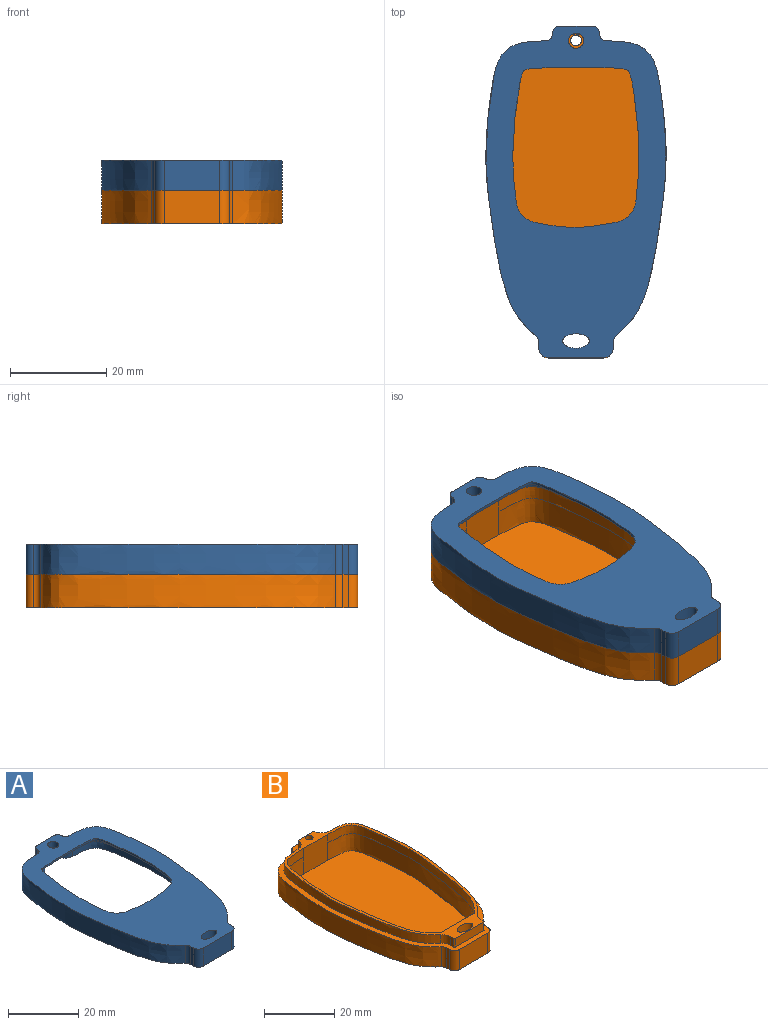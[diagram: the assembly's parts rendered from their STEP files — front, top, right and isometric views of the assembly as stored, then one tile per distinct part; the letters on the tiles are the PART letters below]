
ASSEMBLY  parts=2 mates=1
PART A: 47 faces, bbox 37.5x69.1x6.3 mm
  f0: extruded ~5.57x3.3mm, area 45.3mm2, adj f31,f46
  f1: plane 9.59x2.7mm, normal (0,-1,0), area 25.9mm2, adj f2,f4,f26,f46
  f2: extruded ~56.9x11.37mm, area 179.6mm2, adj f1,f3,f26,f46
  f3: plane 13.49x2.7mm, normal (0,1,0), area 36.4mm2, adj f2,f4,f26,f46
  f4: extruded ~56.9x11.37mm, area 179.6mm2, adj f1,f3,f26,f46
  f5: plane 6.3x1.11mm, normal (-1,0,0), area 7mm2, adj f19,f21,f29,f31
  f6: plane 6.3x1.11mm, normal (1,0,0), area 7mm2, adj f20,f21,f30,f31
  f7: plane 6.3x0.06mm, normal (1,0,0), area 0.4mm2, adj f16,f21,f27,f31
  f8: plane 6.3x0.06mm, normal (-1,0,0), area 0.4mm2, adj f17,f21,f28,f31
  f9: plane 6.3x0.09mm, normal (0.67,-0.74,0), area 0.8mm2, adj f20,f21,f24,f31
  f10: cylinder r=5mm len=4.24mm, axis (0,0,1), area 3.7mm2, adj f11,f15,f26,f31
  f11: extruded ~28x8.43mm, area 20.3mm2, adj f10,f12,f26,f31
  f12: plane 9.48x0.6mm, normal (0,-1,0), area 5.7mm2, adj f11,f13,f26,f31
  f13: extruded ~28.08x8.43mm, area 20.4mm2, adj f12,f14,f26,f31
  f14: cylinder r=5mm len=4.25mm, axis (0,0,1), area 3.7mm2, adj f13,f15,f26,f31
  f15: extruded ~17.03x1.09mm, area 10.3mm2, adj f10,f14,f26,f31
  f16: cylinder r=1.5mm len=6.3mm, axis (0,0,1), area 14.4mm2, adj f7,f21,f24,f31
  f17: cylinder r=1.5mm len=6.3mm, axis (0,0,1), area 14.4mm2, adj f8,f21,f25,f31
  f18: cylinder r=1.59mm len=6.3mm, axis (0,0,1), area 37.9mm2, adj f21,f31,f32,f45,f46
  f19: cylinder r=2mm len=6.3mm, axis (0,0,1), area 10.5mm2, adj f5,f21,f25,f31
  f20: cylinder r=2mm len=6.3mm, axis (0,0,1), area 10.5mm2, adj f6,f9,f21,f31
  f21: plane 69.1x37.55mm, normal (0,0,-1), area 298.6mm2, adj f5,f6,f7,f8,f9,f16,f17,f18
  f22: plane 11.49x6.3mm, normal (0,-1,0), area 72.4mm2, adj f21,f29,f30,f31
  f23: plane 6.69x6.3mm, normal (0,1,0), area 42.2mm2, adj f21,f27,f28,f31
  f24: extruded ~61.37x12.49mm, area 449mm2, adj f9,f16,f21,f31
  f25: extruded ~61.45x12.49mm, area 449.8mm2, adj f17,f19,f21,f31
  f26: plane 56.9x32.93mm, normal (0,0,-1), area 800.2mm2, adj f1,f2,f3,f4,f10,f11,f12,f13
  f27: cylinder r=1.5mm len=6.3mm, axis (0,0,1), area 14.8mm2, adj f7,f21,f23,f31
  f28: cylinder r=1.5mm len=6.3mm, axis (0,0,-1), area 14.8mm2, adj f8,f21,f23,f31
  f29: cylinder r=2mm len=6.3mm, axis (0,0,1), area 19.8mm2, adj f5,f21,f22,f31
  f30: cylinder r=2mm len=6.3mm, axis (0,0,-1), area 19.8mm2, adj f6,f21,f22,f31
  f31: plane 69.1x37.55mm, normal (0,0,1), area 1295.9mm2, adj f0,f5,f6,f7,f8,f9,f10,f11
  f32: plane 3x2.36mm, normal (0,-1,0), area 7.1mm2, adj f18,f21,f33,f46
  f33: cylinder r=3.19mm len=3.06mm, axis (0,0,-1), area 14.2mm2, adj f21,f32,f34,f46
  f34: extruded ~58.43x10.87mm, area 201.8mm2, adj f21,f33,f35,f46
  f35: plane 3x0.09mm, normal (-0.67,0.74,0), area 0.4mm2, adj f21,f34,f36,f46
  f36: cylinder r=3.69mm len=3mm, axis (0,0,-1), area 9.2mm2, adj f21,f35,f37,f46
  f37: plane 3x1.11mm, normal (-1,0,0), area 3.3mm2, adj f21,f36,f38,f46
  f38: cylinder r=0.31mm len=3mm, axis (0,0,-1), area 1.5mm2, adj f21,f37,f39,f46
  f39: plane 11.49x3mm, normal (0,1,0), area 34.5mm2, adj f21,f38,f40,f46
  f40: cylinder r=0.31mm len=3mm, axis (0,0,-1), area 1.5mm2, adj f21,f39,f41,f46
  f41: plane 3x1.11mm, normal (1,0,0), area 3.3mm2, adj f21,f40,f42,f46
  f42: cylinder r=3.69mm len=3mm, axis (0,0,-1), area 9.2mm2, adj f21,f41,f43,f46
  f43: extruded ~58.51x10.87mm, area 202.2mm2, adj f21,f42,f44,f46
  f44: cylinder r=3.19mm len=3.06mm, axis (0,0,-1), area 14.2mm2, adj f21,f43,f45,f46
  f45: plane 3x2.36mm, normal (0,-1,0), area 7.1mm2, adj f18,f21,f44,f46
  f46: plane 65.72x34.17mm, normal (0,0,-1), area 197.1mm2, adj f0,f1,f2,f3,f4,f18,f32,f33
PART B: 42 faces, bbox 37.5x69.1x10 mm
  f0: plane 69.1x37.55mm, normal (0,0,1), area 300.5mm2, adj f1,f3,f4,f5,f6,f7,f8,f9
  f1: plane 7x0.06mm, normal (1,0,0), area 0.4mm2, adj f0,f2,f8,f11
  f2: plane 69.1x37.55mm, normal (0,0,-1), area 2111mm2, adj f1,f3,f4,f5,f6,f7,f8,f9
  f3: plane 7x0.06mm, normal (-1,0,0), area 0.4mm2, adj f0,f2,f9,f10
  f4: plane 7x6.69mm, normal (0,1,0), area 46.8mm2, adj f0,f2,f8,f9
  f5: extruded ~61.37x12.49mm, area 498.9mm2, adj f0,f2,f6,f11
  f6: plane 7x0.09mm, normal (0.67,-0.74,0), area 0.8mm2, adj f0,f2,f5,f19
  f7: extruded ~61.45x12.49mm, area 499.7mm2, adj f0,f2,f10,f20
  f8: cylinder r=1.5mm len=7mm, axis (0,0,1), area 16.5mm2, adj f0,f1,f2,f4
  f9: cylinder r=1.5mm len=7mm, axis (0,0,-1), area 16.5mm2, adj f0,f2,f3,f4
  f10: cylinder r=1.5mm len=7mm, axis (0,0,1), area 16mm2, adj f0,f2,f3,f7
  f11: cylinder r=1.5mm len=7mm, axis (0,0,1), area 16mm2, adj f0,f1,f2,f5
  f12: cylinder r=1.12mm len=10mm, axis (0,0,1), area 70.3mm2, adj f2,f36
  f13: plane 7x1.11mm, normal (-1,0,0), area 7.8mm2, adj f0,f2,f17,f20
  f14: plane 7x1.11mm, normal (1,0,0), area 7.8mm2, adj f0,f2,f18,f19
  f15: plane 11.49x7mm, normal (0,-1,0), area 80.5mm2, adj f0,f2,f17,f18
  f16: extruded ~10x5.57mm, area 137.3mm2, adj f2,f36
  f17: cylinder r=2mm len=7mm, axis (0,0,1), area 22mm2, adj f0,f2,f13,f15
  f18: cylinder r=2mm len=7mm, axis (0,0,-1), area 22mm2, adj f0,f2,f14,f15
  f19: cylinder r=2mm len=7mm, axis (0,0,1), area 11.7mm2, adj f0,f2,f6,f14
  f20: cylinder r=2mm len=7mm, axis (0,0,1), area 11.7mm2, adj f0,f2,f7,f13
  f21: plane 3x1.11mm, normal (1,0,0), area 3.3mm2, adj f0,f22,f35,f36
  f22: cylinder r=3.7mm len=3mm, axis (0,0,-1), area 9.3mm2, adj f0,f21,f23,f36
  f23: plane 3x0.09mm, normal (0.67,-0.74,0), area 0.4mm2, adj f0,f22,f24,f36
  f24: extruded ~58.41x10.86mm, area 201.7mm2, adj f0,f23,f25,f36
  f25: cylinder r=3.2mm len=3.06mm, axis (0,0,-1), area 14.2mm2, adj f0,f24,f26,f36
  f26: plane 6.3x3mm, normal (0,1,0), area 18.9mm2, adj f0,f25,f27,f36
  f27: cylinder r=3.2mm len=3.06mm, axis (0,0,-1), area 14.2mm2, adj f0,f26,f28,f36
  f28: extruded ~58.49x10.86mm, area 202.1mm2, adj f0,f27,f29,f36
  f29: cylinder r=3.7mm len=3mm, axis (0,0,-1), area 9.3mm2, adj f0,f28,f30,f36
  f30: plane 3x1.11mm, normal (-1,0,0), area 3.3mm2, adj f0,f29,f31,f36
  f31: cylinder r=0.3mm len=3mm, axis (0,0,-1), area 1.4mm2, adj f0,f30,f32,f36
  f32: plane 11.49x3mm, normal (0,-1,0), area 34.5mm2, adj f0,f31,f35,f36
  f33: extruded ~56.9x11.37mm, area 199.5mm2, adj f36,f39,f40,f41
  f34: extruded ~56.9x11.37mm, area 199.5mm2, adj f36,f38,f39,f41
  f35: cylinder r=0.3mm len=3mm, axis (0,0,-1), area 1.4mm2, adj f0,f21,f32,f36
  f36: plane 65.7x34.15mm, normal (0,0,1), area 199.1mm2, adj f12,f16,f21,f22,f23,f24,f25,f26
  f37: plane 56.9x32.93mm, normal (0,0,1), area 1611.4mm2, adj f38,f39,f40,f41
  f38: extruded ~56.9x11.37mm, area 399mm2, adj f34,f37,f39,f41
  f39: plane 13.49x9mm, normal (0,1,0), area 121.4mm2, adj f33,f34,f36,f37,f38,f40
  f40: extruded ~56.9x11.37mm, area 399mm2, adj f33,f37,f39,f41
  f41: plane 9.59x9mm, normal (0,-1,0), area 86.3mm2, adj f33,f34,f36,f37,f38,f40
PLACE A t=(-11.17,-4.28,6.35)mm
PLACE B t=(-11.17,-4.28,36.35)mm
MATE fastened B.f36 <-> A.f46  axis (0,0,1) through (-11.17,-35.81,2.35)mm
